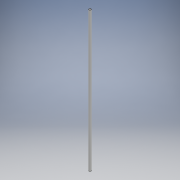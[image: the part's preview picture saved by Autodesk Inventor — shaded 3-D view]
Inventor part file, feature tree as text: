
AUTODESK INVENTOR PART (.ipt)
format: ipt  version: 2018 (Build 220112000, 112)  size: 94,208 bytes
history: native  units: mm
features: extrude x2, sketch x2, other x1
ambient origin geometry x8: Origin, YZ Plane, XZ Plane, XY Plane, X Axis, Y Axis, Z Axis, Center Point
bodies: Body1 (feature_tree)
feature tree (5):
  other  "ソリッド1"
  extrude  "押し出し1"  Depth=27.2mm
  extrude  "押し出し2"  Depth=1700.0mm TaperAngle=0.0deg
  sketch  "スケッチ1"
  sketch  "スケッチ2"
